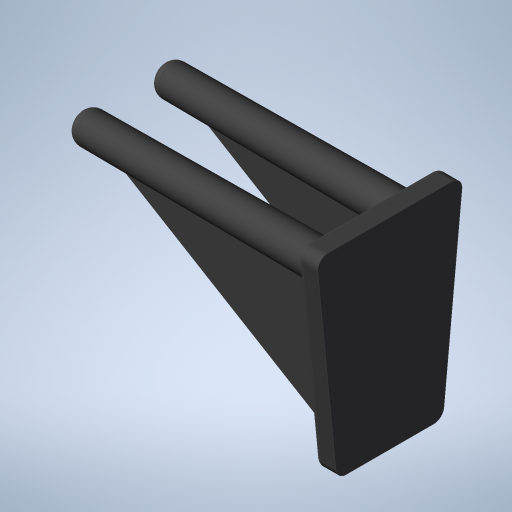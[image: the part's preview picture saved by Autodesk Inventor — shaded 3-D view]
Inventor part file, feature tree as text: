
AUTODESK INVENTOR PART (.ipt)
format: ipt  version: 2023 (Build 270158000, 158)  size: 319,488 bytes
history: native  units: in
note: dims shown in document units (in); Inventor stores cm internally (conversion verified against a paired STEP export)
features: extrude x4, fillet x3, sketch x2, draft x2, chamfer x1
ambient origin geometry x8: Origin, YZ Plane, XZ Plane, XY Plane, X Axis, Y Axis, Z Axis, Center Point
bodies: Body1 (feature_tree)
feature tree (12):
  sketch  "Sketch3"  dims[d14=0.0625in d15=0.125in]
  extrude  "Extrusion2"  Depth=0.125in
  extrude  "Extrusion3"  Depth=0.125in TaperAngle=0.0deg
  extrude  "Extrusion4"  Depth=5.0in TaperAngle=0.0deg
  extrude  "Extrusion5"  Depth=5.0in TaperAngle=0.0deg
  draft  "FaceDraft2"
  draft  "FaceDraft3"
  fillet  "Fillet3"  Radius=0.0027in
  fillet  "Fillet5"  Radius=0.0027in
  fillet  "Fillet6"  Radius=0.25in
  chamfer  "Chamfer1"  Distance=0.25in
  sketch  "Sketch4"  dims[d25=0.5in d26=0.0in d27=6.0in d28=0.0in d29=5.0in d30=0.0in d31=5.0in d32=0.0in d36=0.0027in d37=0.0027in d38=0.25in d40=0.25in d41=0.25in d42=0.125in d43=0.0417in d44=0.125in d45=45.0deg]
